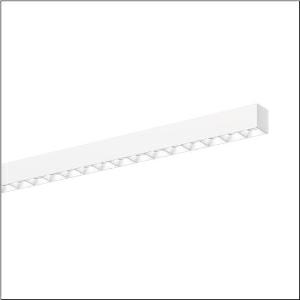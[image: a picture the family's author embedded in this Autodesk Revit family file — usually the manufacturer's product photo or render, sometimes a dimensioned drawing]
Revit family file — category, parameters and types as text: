
# Revit family: silica_21_51mx26db35wb
name_source: partatom
category: Lighting Fixtures
units: mm (PartAtom-declared; Revit-internal decimal feet)

## family parameters
Cut with Voids When Loaded = No
Host = Face
Light Source = No
Part Type = Normal
Room Calculation Point = No
Round Connector Dimension = Use Diameter
Shared = No

## types (1)
- --- (1 x LED, 5400 lm, 31.4 W, 3000K)
    Apparent Load = 31 VA
    CIE Flux Codes = 83 98 100 100 100
    Color Rendering = 80
    Color Temperature = 3000K
    Default Elevation = 1800 mm
    Description = Silica 21, office luminaire, primary light control with darklight reflector, of PMMA, white, CAT 2 (L<= 3000cd/m²), light emission: direct distribution, primary light characteristic: symmetric, installation type: surface-mounted, LED, rated luminous flux: 5.400lm, luminous efficacy: 172lm/W, light colour: 830, colour temperature: 3000K, control gear: DALI 2, with terminal, 3+2-pole, max. 2.5mm², mains connection: 220..240V, AC, 50/60Hz, rated input power: 31.4W, luminaire housing, of aluminium, traffic white (RAL 9016), length: 1.504mm, width: 53mm, height: 53mm, protection rating (complete): IP20, insulation class (complete): insulation class I (protective earthing), certification: CE, permissible operating ambient temperature: 0..+35°C, standard: EN 50419, packaging unit: 1 piece
    Height = 53 mm
    Lamp = 1 x LED
    Lamp Light Flux = 5400 lm
    Lamp Power = 31.4 W
    Lamp count = 1
    Length = 1504 mm
    Luminous efficacy = 172 lm/W
    Manufacturer = Siteco
    ModVariant = No
    Model = 51MX26DB35WB
    Mounting Place = Ceiling
    Mounting Type = Surface mounted
    Number of Poles = 1
    OnlyDefault = Yes
    Power Factor = 1
    Product Name = Silica 21
    Product group = office luminaire | ceiling mounted
    ProductGroupID = 301
    Protection Class = Protection class I
    Protection Degree = IP 20
    RLX_Detail_Level = 1
    RLX_Emergency_Light_Flux = 0 lm
    RLX_Emergency_Type = 0
    RLX_Emergency_Type_DB = No
    RlxData = <blob elided: 41925 chars, md5=804fcd23>
    Socket = socket
    Standby Power = 0 W
    System Light Flux = 5400 lm
    System Power = 31 W
    Type Comments = factory setting: luminous flux: 100 % | dim-lin: 254 | 360 mA
    Type Image = l_1335934.jpg
    URL = http://relux.com
    VarID = @adj_125975
    Voltage = 0 V
    Weight = 0.00 kg
    Width = 53 mm

## geometry (parser evidence)
native form markers: Blend x4, Sweep x9
no freeform markers — native parametric forms only
